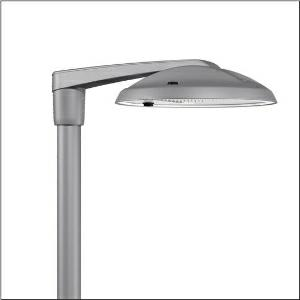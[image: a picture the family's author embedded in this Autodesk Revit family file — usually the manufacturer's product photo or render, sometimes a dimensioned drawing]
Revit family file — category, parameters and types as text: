
# Revit family: dl_r__50_iq_mini___st1_0a_5xa248d31y08le_5d77
name_source: partatom
category: Lighting Fixtures
units: mm (PartAtom-declared; Revit-internal decimal feet)

## family parameters
Cut with Voids When Loaded = No
Host = Face
Light Source = No
Part Type = Normal
Room Calculation Point = No
Round Connector Dimension = Use Diameter
Shared = No

## types (1)
- --- (1 x LED, 10390 lm, 66 W, 3000K)
    Apparent Load = 66 VA
    CIE Flux Codes = 37 72 97 100 100
    Color Rendering = 70
    Color Temperature = 3000K
    Default Elevation = 1800 mm
    Description = DL® 50 iQ mini, mast luminaire, primary light control with lens, of PMMA, primary optical cover: cover, of toughened safety glass, transparent, light distribution: ST1.0a, light emission: direct distribution, primary light characteristic: asymmetric, installation type: post-top, side-entry, LED, High Power LED, rated luminous flux: 10.390lm, luminous efficacy: 157lm/W, light colour: 730, colour temperature: 3000K, control gear: iQ-Street Remote, D4i with power reduction, control: optimised constant luminous flux control (CLO 2.0), Desk-Remote (wireless, voltage-free reading and setting of iQ features in the workshop via application-optimized NFC function/RFID function), Light-Fading, Smart-Wire, Night-Set, Lumen-Switch, Temp-Guard, Auto-Match, Street-Remote, pre-setting: logarithmic dimming characteristic, mains connection: 230..240V, AC, 50/60Hz, connection cable pre-assembled, cable length: 8,5m, start of lifetime: 66W, end of service life: 69W, reduction: 30W, luminaire housing, of diecast aluminium, powder-coated, Siteco® metallic grey (DB 702S), inclination adjustable: 0°, 5°, 10° (post-top) | 0°, -5°, -10°, -15° (side-entry), please order mast post-top element or mast side-entry element separately, diameter: 500mm, height: 115mm, post-top: for spigot size d x l = 76 x 100mm; with reducer (optional accessory) 60 x 100mm | side-entry: for spigot size d x l = 60 x 100mm; with reducer (optional accessory) 42 x 100mm, mounting height: 4..6m, Smart Interface below and above, protection rating (complete): IP66, insulation class (complete): insulation class II (safety insulation), certification: CE, ENEC, ENEC+, VDE, impact resistance: IK08, permissible operating ambient temperature for outdoor applications: -25..+40°C, standard-compliant lighting for roads and squares, packaging unit: 1 piece

Light Distribution: ST1.0a
    Height = 115 mm
    Lamp = 1 x LED
    Lamp Light Flux = 10390 lm
    Lamp Power = 66 W
    Lamp count = 1
    Length = 500 mm
    Luminous efficacy = 157 lm/W
    Manufacturer = Siteco
    ModVariant = No
    Model = 5XA248D31Y08LE
    Number of Poles = 1
    OnlyDefault = Yes
    Power Factor = 1
    Product Name = DL® 50 iQ mini | ST1.0a
    Product group = mast luminaire | pylon top
    ProductGroupID = 6100
    Protection Class = Protection class II
    Protection Degree = IP 66
    RLX_Detail_Level = 1
    RLX_Emergency_Light_Flux = 0 lm
    RLX_Emergency_Type = 0
    RLX_Emergency_Type_DB = No
    RlxData = <blob elided: 107257 chars, md5=0f0f84ae>
    Socket = socket
    Standby Power = 0 W
    System Light Flux = 10390 lm
    System Power = 66 W
    Type Comments = factory setting: luminous flux: 100 % | dim-lin: 254 | 691 mA
    Type Image = l_1251786.jpg
    URL = http://relux.com
    VarID = @adj_065628
    Voltage = 0 V
    Weight = 0.00 kg
    Width = 0 mm  [stored 0 ft]

note: [stored X ft] marks values corroborated as IEEE doubles in the binary element streams (Revit-internal decimal feet)

## geometry (parser evidence)
native form markers: Blend x4, Sweep x8
no freeform markers — native parametric forms only
